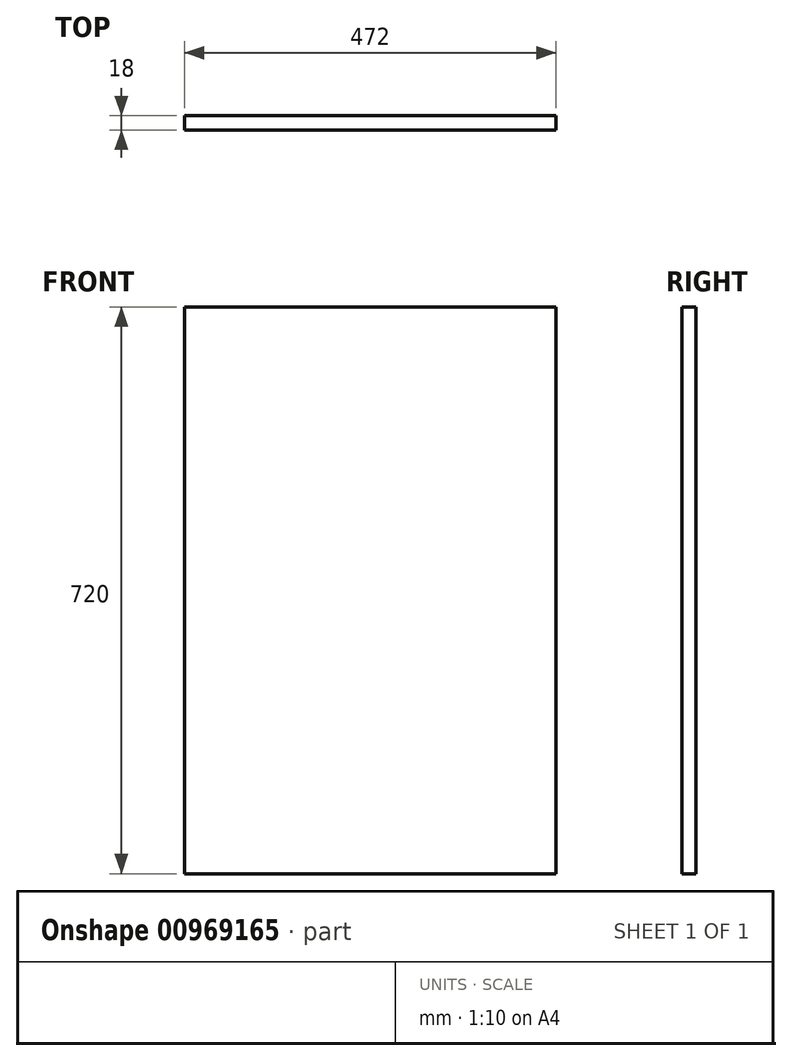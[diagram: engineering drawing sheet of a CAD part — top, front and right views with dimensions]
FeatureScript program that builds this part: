
annotation { "Feature Type Name" : "Feature", "Feature Type Description" : "" }
export const myFeature = defineFeature(function(context is Context, id is Id, definition is map)
    precondition{}
    {
        {
            var Q0;
            Q0=qCreatedBy(makeId("Front.planeOp"),FACE);
            var sketch = newSketch(context, id + "F0", { "sketchPlane" : qUnion([Q0])});
            skLineSegment(sketch, "E0.bottom", {"start": v(0, 0) * mm, "end": v(472, 0) * mm});
            skLineSegment(sketch, "E0.top", {"start": v(0, 720) * mm, "end": v(472, 720) * mm});
            skLineSegment(sketch, "E0.left", {"start": v(0, 0) * mm, "end": v(0, 720) * mm});
            skLineSegment(sketch, "E0.right", {"start": v(472, 0) * mm, "end": v(472, 720) * mm});
            skSolve(sketch);
        }
        {
            var Q0;
            Q0 = qSketchRegion(id + "F0", true);
            extrude(context, id + "F1", {"entities" : qUnion([Q0]), "depth" : 18 * mm, "offsetDistance" : 25 * mm});
        }
    });
